# Revit family: EU_SINGLE_IDU_SLIM DUCT S
name_source: partatom
category: Mechanical Equipment
revit_build: Autodesk Revit 2016 (Build: 20150220_1215(x64)
units: mm (PartAtom-declared; Revit-internal decimal feet)

## family parameters
Always vertical = Yes
Cut with Voids When Loaded = No
Part Type = Normal
Room Calculation Point = No
Round Connector Dimension = Use Radius
Shared = No
Work Plane-Based = No

## types (2) — shared parameters
Clearance Offset Back = 0.00 mm
Clearance Offset Bottom = 0.00 mm
Clearance Offset Front = 0.00 mm
Clearance Offset Left = 0.00 mm
Clearance Offset Right = 0.00 mm
Clearance Offset Top = 0.00 mm
Clearance Type = Do not Include Clearance
Family Load Status = Valid - Type loaded via type catalog
Manufacturer = SAMSUNG
Motor Output = 68 W
Net Weight = 19.40 kg
Panel Net Weight = 0.00 kg
Refrigerant Type = R410A
URL = www.samsung.com

## per-type parameters (varying)
| type | Model |
| 2.60 kW, 220-240V, SLIM DUCT | AC026MNLDKH/EU |
| 3.50 kW, 220-240V, SLIM DUCT | AC035MNLDKH/EU |

## geometry (parser evidence)
native form markers: Sweep x6
no freeform markers — native parametric forms only
